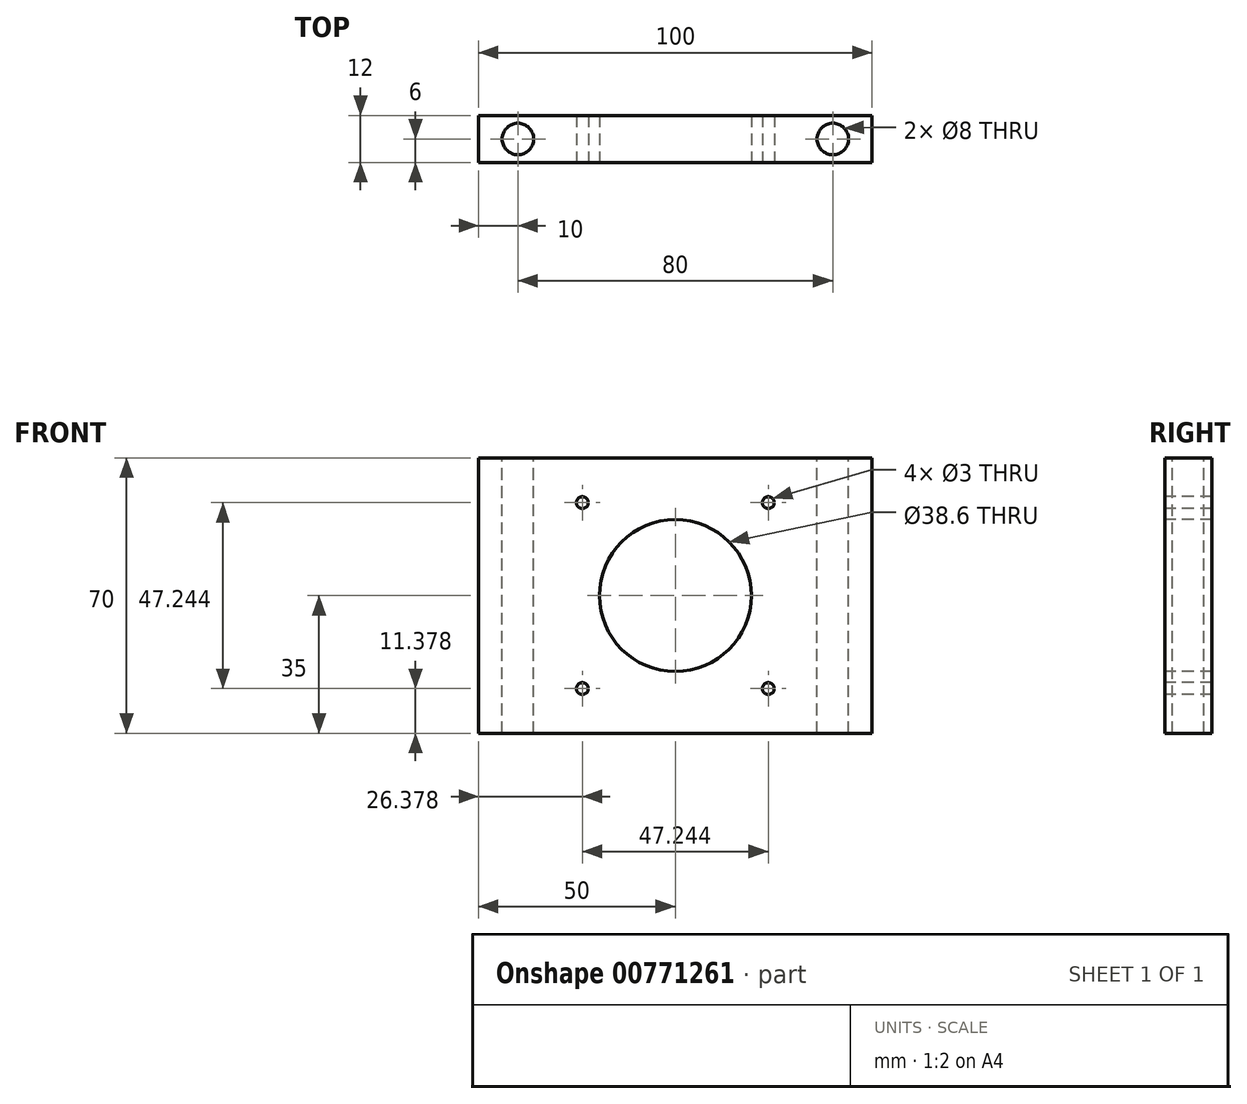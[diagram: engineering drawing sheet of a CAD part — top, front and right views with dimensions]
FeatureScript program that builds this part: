
annotation { "Feature Type Name" : "Feature", "Feature Type Description" : "" }
export const myFeature = defineFeature(function(context is Context, id is Id, definition is map)
    precondition{}
    {
        {
            var Q0;
            Q0=qCreatedBy(makeId("Front.planeOp"),FACE);
            var sketch = newSketch(context, id + "F0", { "sketchPlane" : qUnion([Q0])});
            skLineSegment(sketch, "E0.bottom", {"start": v(50, -35) * mm, "end": v(-50, -35) * mm});
            skLineSegment(sketch, "E0.top", {"start": v(50, 35) * mm, "end": v(-50, 35) * mm});
            skLineSegment(sketch, "E0.left", {"start": v(50, -35) * mm, "end": v(50, 35) * mm});
            skLineSegment(sketch, "E0.right", {"start": v(-50, -35) * mm, "end": v(-50, 35) * mm});
            skPoint(sketch, "E0.middle", {"position": v(0, 0) * mm});
            skSolve(sketch);
        }
        {
            var Q0;
            Q0 = qSketchRegion(id + "F0", true);
            extrude(context, id + "F1", {"entities" : qUnion([Q0]), "depth" : 12 * mm, "offsetDistance" : 25 * mm});
        }
        {
            var Q0;
            Q0=makeQuery(id+"F1.opExtrude","CAP_FACE",FACE,{"disambiguationData":[OSD([sQuery(id+"F0.wireOp",EDGE,"E0.bottom"),sQuery(id+"F0.wireOp",EDGE,"E0.top"),sQuery(id+"F0.wireOp",EDGE,"E0.left"),sQuery(id+"F0.wireOp",EDGE,"E0.right")])],"isStart":false});
            var sketch = newSketch(context, id + "F2", { "sketchPlane" : qUnion([Q0])});
            skCircle(sketch, "E1", {"center": v(0, 0) * mm, "radius": 19.3 * mm});
            skLineSegment(sketch, "E2.bottom", {"start": v(-23.62, 23.62) * mm, "end": v(23.62, 23.62) * mm, "construction": true});
            skLineSegment(sketch, "E2.top", {"start": v(-23.62, -23.62) * mm, "end": v(23.62, -23.62) * mm, "construction": true});
            skLineSegment(sketch, "E2.left", {"start": v(-23.62, 23.62) * mm, "end": v(-23.62, -23.62) * mm, "construction": true});
            skLineSegment(sketch, "E2.right", {"start": v(23.62, 23.62) * mm, "end": v(23.62, -23.62) * mm, "construction": true});
            skCircle(sketch, "E3", {"center": v(-23.62, 23.62) * mm, "radius": 1.5 * mm});
            skCircle(sketch, "E4", {"center": v(23.62, 23.62) * mm, "radius": 1.5 * mm});
            skCircle(sketch, "E5", {"center": v(23.62, -23.62) * mm, "radius": 1.5 * mm});
            skCircle(sketch, "E6", {"center": v(-23.62, -23.62) * mm, "radius": 1.5 * mm});
            skSolve(sketch);
        }
        {
            var Q0;
            Q0 = qSketchRegion(id + "F2", true);
            extrude(context, id + "F3", {"entities" : qUnion([Q0]), "operationType" : NewBodyOperationType.REMOVE, "endBound" : BoundingType.THROUGH_ALL, "oppositeDirection" : true, "depth" : 25 * mm, "offsetDistance" : 25 * mm});
        }
        {
            var Q0;
            Q0=makeQuery(id+"F1.opExtrude","SWEPT_FACE",FACE,{"disambiguationData":[OSD([sQuery(id+"F0.wireOp",EDGE,"E0.top")])]});
            var sketch = newSketch(context, id + "F4", { "sketchPlane" : qUnion([Q0])});
            skLineSegment(sketch, "E7", {"start": v(-50, -6) * mm, "end": v(50, -6) * mm, "construction": true});
            skPoint(sketch, "E8", {"position": v(-40, -6) * mm});
            skPoint(sketch, "E9", {"position": v(40, -6) * mm});
            skLineSegment(sketch, "E10", {"start": v(0, 0) * mm, "end": v(0, -12) * mm, "construction": true});
            skSolve(sketch);
        }
        {
            var Q0;
            Q0=sQuery(id+"F4.wireOp",VERTEX,"E8");
            var Q1;
            Q1=sQuery(id+"F4.wireOp",VERTEX,"E9");
            var Q2;
            Q2=makeQuery(id+"F1.opExtrude","SWEPT_BODY",BODY,{"disambiguationData":[OSD([sQuery(id+"F0.wireOp",EDGE,"E0.bottom"),sQuery(id+"F0.wireOp",EDGE,"E0.top"),sQuery(id+"F0.wireOp",EDGE,"E0.left"),sQuery(id+"F0.wireOp",EDGE,"E0.right")])]});
            hole(context, id + "F5", {"style" : HoleStyle.SIMPLE, "endStyle" : HoleEndStyle.THROUGH, "holeDiameter" : 8 * mm, "majorDiameter" : 5 * mm, "isTappedThrough" : true, "tappedDepth" : 12 * mm, "tapClearance" : 3, "locations" : qUnion([Q0, Q1]), "scope" : qUnion([Q2])});
        }
    });
